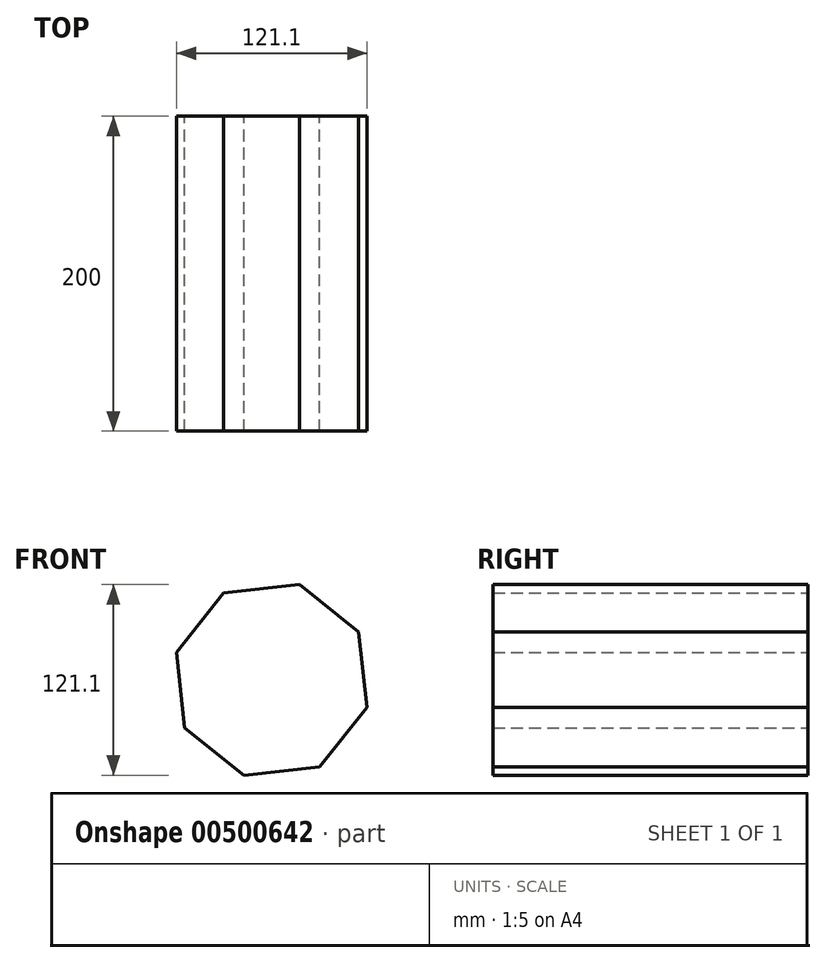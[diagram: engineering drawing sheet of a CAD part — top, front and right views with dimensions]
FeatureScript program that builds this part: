
annotation { "Feature Type Name" : "Feature", "Feature Type Description" : "" }
export const myFeature = defineFeature(function(context is Context, id is Id, definition is map)
    precondition{}
    {
        {
            var Q0;
            Q0=qCreatedBy(makeId("Front.planeOp"),FACE);
            var sketch = newSketch(context, id + "F0", { "sketchPlane" : qUnion([Q0])});
            skCircle(sketch, "E0.cCircle", {"center": v(0, 0) * mm, "radius": 63.04 * mm, "construction": true});
            skLineSegment(sketch, "E0.0", {"start": v(-30.4, 55.23) * mm, "end": v(17.55, 60.55) * mm});
            skLineSegment(sketch, "E0.1", {"start": v(17.55, 60.55) * mm, "end": v(55.23, 30.4) * mm});
            skLineSegment(sketch, "E0.2", {"start": v(55.23, 30.4) * mm, "end": v(60.55, -17.55) * mm});
            skLineSegment(sketch, "E0.3", {"start": v(60.55, -17.55) * mm, "end": v(30.4, -55.23) * mm});
            skLineSegment(sketch, "E0.4", {"start": v(30.4, -55.23) * mm, "end": v(-17.55, -60.55) * mm});
            skLineSegment(sketch, "E0.5", {"start": v(-17.55, -60.55) * mm, "end": v(-55.23, -30.4) * mm});
            skLineSegment(sketch, "E0.6", {"start": v(-55.23, -30.4) * mm, "end": v(-60.55, 17.55) * mm});
            skLineSegment(sketch, "E0.7", {"start": v(-60.55, 17.55) * mm, "end": v(-30.4, 55.23) * mm});
            skSolve(sketch);
        }
        {
            var Q0;
            Q0=makeQuery(id+"F0.imprint","IMPRINT",FACE,{"disambiguationData":[TD([[makeQuery(id+"F0.imprint","IMPRINT",EDGE,{"derivedFrom":sQuery(id+"F0.wireOp",EDGE,"E0.0")}),-1.0]])]});
            extrude(context, id + "F1", {"entities" : qUnion([Q0]), "depth" : 200 * mm});
        }
    });
